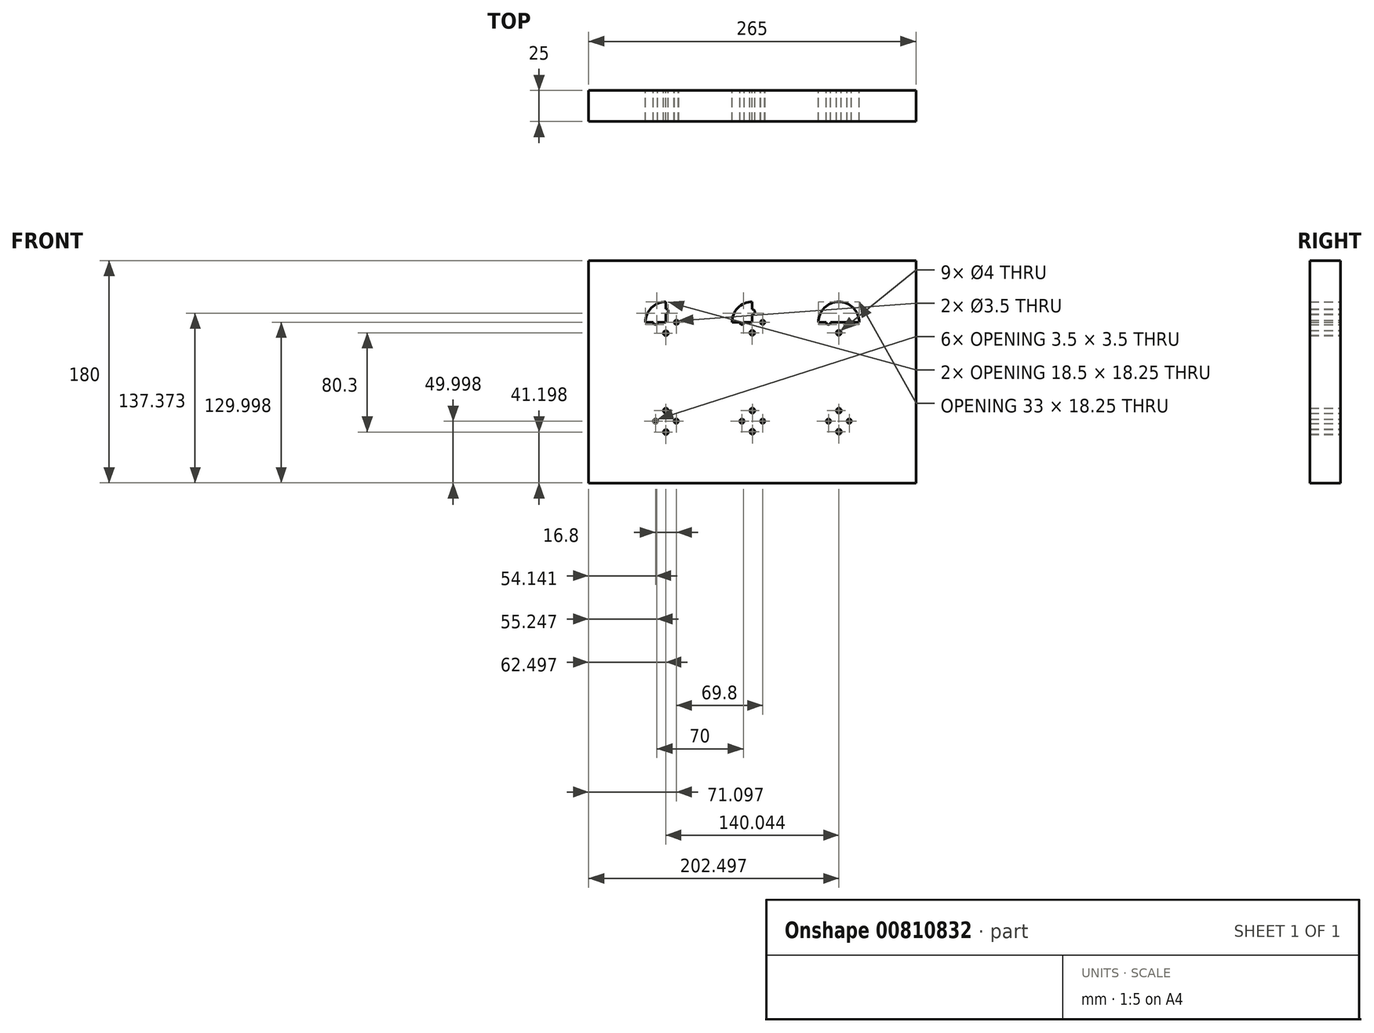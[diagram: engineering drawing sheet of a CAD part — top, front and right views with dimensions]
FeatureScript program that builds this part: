
annotation { "Feature Type Name" : "Feature", "Feature Type Description" : "" }
export const myFeature = defineFeature(function(context is Context, id is Id, definition is map)
    precondition{}
    {
        {
            var Q0;
            Q0=qCreatedBy(makeId("Front.planeOp"),FACE);
            var sketch = newSketch(context, id + "F0", { "sketchPlane" : qUnion([Q0])});
            skLineSegment(sketch, "E0.bottom", {"start": v(-104.92, 118.45) * mm, "end": v(160.08, 118.45) * mm});
            skLineSegment(sketch, "E0.top", {"start": v(-104.92, -61.55) * mm, "end": v(160.08, -61.55) * mm});
            skLineSegment(sketch, "E0.left", {"start": v(-104.92, 118.45) * mm, "end": v(-104.92, -61.55) * mm});
            skLineSegment(sketch, "E0.right", {"start": v(160.08, 118.45) * mm, "end": v(160.08, -61.55) * mm});
            skLineSegment(sketch, "E1", {"start": v(-42.42, 118.45) * mm, "end": v(-42.42, -61.55) * mm});
            skLineSegment(sketch, "E2", {"start": v(27.58, 118.45) * mm, "end": v(27.58, -61.55) * mm});
            skLineSegment(sketch, "E3", {"start": v(97.58, 118.45) * mm, "end": v(97.58, -61.55) * mm});
            skLineSegment(sketch, "E4", {"start": v(-104.92, 68.45) * mm, "end": v(160.08, 68.45) * mm});
            skLineSegment(sketch, "E5", {"start": v(-104.92, -11.55) * mm, "end": v(160.08, -11.55) * mm});
            skCircle(sketch, "E6", {"center": v(-42.42, 68.45) * mm, "radius": 16.5 * mm});
            skCircle(sketch, "E7", {"center": v(-33.82, 68.45) * mm, "radius": 1.75 * mm});
            skCircle(sketch, "E8", {"center": v(-50.82, 68.45) * mm, "radius": 1.75 * mm});
            skCircle(sketch, "E9", {"center": v(-42.42, 59.65) * mm, "radius": 2 * mm});
            skCircle(sketch, "E10", {"center": v(-42.42, 77.25) * mm, "radius": 2 * mm});
            skLineSegment(sketch, "E11.direction1", {"start": v(-42.42, 68.45) * mm, "end": v(27.58, 68.45) * mm, "construction": true});
            skLineSegment(sketch, "E11.direction2", {"start": v(-42.42, 68.45) * mm, "end": v(-42.42, -1.55) * mm, "construction": true});
            skCircle(sketch, "E12.0.1.0", {"center": v(-42.38, -11.55) * mm, "radius": 16.5 * mm});
            skCircle(sketch, "E12.0.1.1", {"center": v(-42.38, -3.05) * mm, "radius": 2 * mm});
            skCircle(sketch, "E12.0.1.2", {"center": v(-33.98, -11.55) * mm, "radius": 1.75 * mm});
            skCircle(sketch, "E12.0.1.3", {"center": v(-42.38, -20.35) * mm, "radius": 2 * mm});
            skCircle(sketch, "E12.0.1.4", {"center": v(-50.78, -11.55) * mm, "radius": 1.75 * mm});
            skCircle(sketch, "E12.1.0.0", {"center": v(27.58, 68.45) * mm, "radius": 16.5 * mm});
            skCircle(sketch, "E12.1.0.1", {"center": v(27.58, 76.95) * mm, "radius": 2 * mm});
            skCircle(sketch, "E12.1.0.2", {"center": v(35.98, 68.45) * mm, "radius": 1.75 * mm});
            skCircle(sketch, "E12.1.0.3", {"center": v(27.58, 59.95) * mm, "radius": 2 * mm});
            skCircle(sketch, "E12.1.0.4", {"center": v(19.18, 68.45) * mm, "radius": 1.75 * mm});
            skCircle(sketch, "E12.1.1.0", {"center": v(27.62, -11.55) * mm, "radius": 16.5 * mm});
            skCircle(sketch, "E12.1.1.1", {"center": v(27.62, -3.05) * mm, "radius": 2 * mm});
            skCircle(sketch, "E12.1.1.2", {"center": v(36.02, -11.55) * mm, "radius": 1.75 * mm});
            skCircle(sketch, "E12.1.1.3", {"center": v(27.62, -20.05) * mm, "radius": 2 * mm});
            skCircle(sketch, "E12.1.1.4", {"center": v(19.22, -11.55) * mm, "radius": 1.75 * mm});
            skCircle(sketch, "E12.2.0.0", {"center": v(97.58, 68.45) * mm, "radius": 16.5 * mm});
            skCircle(sketch, "E12.2.0.1", {"center": v(97.58, 76.95) * mm, "radius": 2 * mm});
            skCircle(sketch, "E12.2.0.2", {"center": v(105.98, 68.45) * mm, "radius": 1.75 * mm});
            skCircle(sketch, "E12.2.0.3", {"center": v(97.58, 59.95) * mm, "radius": 2 * mm});
            skCircle(sketch, "E12.2.0.4", {"center": v(89.18, 68.45) * mm, "radius": 1.75 * mm});
            skCircle(sketch, "E12.2.1.0", {"center": v(97.62, -11.55) * mm, "radius": 16.5 * mm});
            skCircle(sketch, "E12.2.1.1", {"center": v(97.62, -3.05) * mm, "radius": 2 * mm});
            skCircle(sketch, "E12.2.1.2", {"center": v(106.02, -11.55) * mm, "radius": 1.75 * mm});
            skCircle(sketch, "E12.2.1.3", {"center": v(97.62, -20.05) * mm, "radius": 2 * mm});
            skCircle(sketch, "E12.2.1.4", {"center": v(89.22, -11.55) * mm, "radius": 1.75 * mm});
            skLineSegment(sketch, "E12.direction2", {"start": v(-42.42, 59.65) * mm, "end": v(-42.38, -20.35) * mm, "construction": true});
            skSolve(sketch);
        }
        {
            var Q0;
            Q0 = qSketchRegion(id + "F0", true);
            var Q1;
            {var subQ5=sQuery(id+"F0.wireOp",EDGE,"E6");var subQ13=sQuery(id+"F0.wireOp",EDGE,"E1");var subQ14=makeQuery(id+"F0.imprint","INTERSECT",VERTEX,{"disambiguationData":[OD(1.0)],"derivedFrom":[subQ13,subQ5]});Q1=makeQuery(id+"F0.imprint","IMPRINT",FACE,{"disambiguationData":[TD([[makeQuery(id+"F0.imprint","IMPRINT",EDGE,{"disambiguationData":[TD([[subQ14,-1.0]])],"derivedFrom":subQ13}),1.0]])]});}
            var Q2;
            {var subQ5=sQuery(id+"F0.wireOp",EDGE,"E12.1.0.0");var subQ13=sQuery(id+"F0.wireOp",EDGE,"E2");var subQ15=makeQuery(id+"F0.imprint","INTERSECT",VERTEX,{"disambiguationData":[OD(1.0)],"derivedFrom":[subQ13,subQ5]});Q2=makeQuery(id+"F0.imprint","IMPRINT",FACE,{"disambiguationData":[TD([[makeQuery(id+"F0.imprint","IMPRINT",EDGE,{"disambiguationData":[TD([[subQ15,-1.0]])],"derivedFrom":subQ13}),1.0]])]});}
            var Q3;
            {var subQ0=sQuery(id+"F0.wireOp",EDGE,"E4");var subQ1=sQuery(id+"F0.wireOp",EDGE,"E3");var subQ2=makeQuery(id+"F0.imprint","INTERSECT",VERTEX,{"derivedFrom":[subQ1,subQ0]});Q3=makeQuery(id+"F0.imprint","IMPRINT",FACE,{"disambiguationData":[TD([[makeQuery(id+"F0.imprint","IMPRINT",EDGE,{"disambiguationData":[TD([[subQ2,-1.0]])],"derivedFrom":subQ1}),-1.0]])]});}
            var Q4;
            {var subQ1=sQuery(id+"F0.wireOp",EDGE,"E3");var subQ5=sQuery(id+"F0.wireOp",EDGE,"E12.2.0.0");var subQ10=makeQuery(id+"F0.imprint","INTERSECT",VERTEX,{"disambiguationData":[OD(0.0)],"derivedFrom":[subQ1,subQ5]});Q4=makeQuery(id+"F0.imprint","IMPRINT",FACE,{"disambiguationData":[TD([[makeQuery(id+"F0.imprint","IMPRINT",EDGE,{"disambiguationData":[TD([[subQ10,-1.0]])],"derivedFrom":subQ1}),-1.0]])]});}
            var Q5;
            {var subQ3=sQuery(id+"F0.wireOp",EDGE,"E12.2.0.0");var subQ6=sQuery(id+"F0.wireOp",EDGE,"E3");var subQ11=makeQuery(id+"F0.imprint","INTERSECT",VERTEX,{"disambiguationData":[OD(0.0)],"derivedFrom":[subQ6,subQ3]});Q5=makeQuery(id+"F0.imprint","IMPRINT",FACE,{"disambiguationData":[TD([[makeQuery(id+"F0.imprint","IMPRINT",EDGE,{"disambiguationData":[TD([[subQ11,-1.0]])],"derivedFrom":subQ6}),1.0]])]});}
            var Q6;
            {var subQ1=sQuery(id+"F0.wireOp",EDGE,"E4");var subQ5=sQuery(id+"F0.wireOp",EDGE,"E3");var subQ6=makeQuery(id+"F0.imprint","INTERSECT",VERTEX,{"derivedFrom":[subQ5,subQ1]});Q6=makeQuery(id+"F0.imprint","IMPRINT",FACE,{"disambiguationData":[TD([[makeQuery(id+"F0.imprint","IMPRINT",EDGE,{"disambiguationData":[TD([[subQ6,-1.0]])],"derivedFrom":subQ5}),1.0]])]});}
            var Q7;
            {var subQ1=sQuery(id+"F0.wireOp",EDGE,"E3");var subQ7=sQuery(id+"F0.wireOp",EDGE,"E12.2.1.0");var subQ8=makeQuery(id+"F0.imprint","INTERSECT",VERTEX,{"disambiguationData":[OD(0.0)],"derivedFrom":[subQ1,subQ7]});Q7=makeQuery(id+"F0.imprint","IMPRINT",FACE,{"disambiguationData":[TD([[makeQuery(id+"F0.imprint","IMPRINT",EDGE,{"disambiguationData":[TD([[subQ8,-1.0]])],"derivedFrom":subQ1}),-1.0]])]});}
            var Q8;
            {var subQ3=sQuery(id+"F0.wireOp",EDGE,"E12.2.1.0");var subQ5=sQuery(id+"F0.wireOp",EDGE,"E3");var subQ10=makeQuery(id+"F0.imprint","INTERSECT",VERTEX,{"disambiguationData":[OD(0.0)],"derivedFrom":[subQ5,subQ3]});Q8=makeQuery(id+"F0.imprint","IMPRINT",FACE,{"disambiguationData":[TD([[makeQuery(id+"F0.imprint","IMPRINT",EDGE,{"disambiguationData":[TD([[subQ10,-1.0]])],"derivedFrom":subQ5}),1.0]])]});}
            var Q9;
            {var subQ1=sQuery(id+"F0.wireOp",EDGE,"E5");var subQ6=sQuery(id+"F0.wireOp",EDGE,"E3");var subQ9=makeQuery(id+"F0.imprint","INTERSECT",VERTEX,{"derivedFrom":[subQ6,subQ1]});Q9=makeQuery(id+"F0.imprint","IMPRINT",FACE,{"disambiguationData":[TD([[makeQuery(id+"F0.imprint","IMPRINT",EDGE,{"disambiguationData":[TD([[subQ9,-1.0]])],"derivedFrom":subQ6}),1.0]])]});}
            var Q10;
            {var subQ0=sQuery(id+"F0.wireOp",EDGE,"E5");var subQ1=sQuery(id+"F0.wireOp",EDGE,"E3");var subQ2=makeQuery(id+"F0.imprint","INTERSECT",VERTEX,{"derivedFrom":[subQ1,subQ0]});Q10=makeQuery(id+"F0.imprint","IMPRINT",FACE,{"disambiguationData":[TD([[makeQuery(id+"F0.imprint","IMPRINT",EDGE,{"disambiguationData":[TD([[subQ2,-1.0]])],"derivedFrom":subQ1}),-1.0]])]});}
            var Q11;
            {var subQ1=sQuery(id+"F0.wireOp",EDGE,"E5");var subQ5=sQuery(id+"F0.wireOp",EDGE,"E2");var subQ6=makeQuery(id+"F0.imprint","INTERSECT",VERTEX,{"derivedFrom":[subQ5,subQ1]});Q11=makeQuery(id+"F0.imprint","IMPRINT",FACE,{"disambiguationData":[TD([[makeQuery(id+"F0.imprint","IMPRINT",EDGE,{"disambiguationData":[TD([[subQ6,-1.0]])],"derivedFrom":subQ5}),1.0]])]});}
            var Q12;
            {var subQ3=sQuery(id+"F0.wireOp",EDGE,"E12.1.1.0");var subQ6=sQuery(id+"F0.wireOp",EDGE,"E2");var subQ10=makeQuery(id+"F0.imprint","INTERSECT",VERTEX,{"disambiguationData":[OD(0.0)],"derivedFrom":[subQ6,subQ3]});Q12=makeQuery(id+"F0.imprint","IMPRINT",FACE,{"disambiguationData":[TD([[makeQuery(id+"F0.imprint","IMPRINT",EDGE,{"disambiguationData":[TD([[subQ10,-1.0]])],"derivedFrom":subQ6}),1.0]])]});}
            var Q13;
            {var subQ1=sQuery(id+"F0.wireOp",EDGE,"E2");var subQ5=sQuery(id+"F0.wireOp",EDGE,"E12.1.1.0");var subQ10=makeQuery(id+"F0.imprint","INTERSECT",VERTEX,{"disambiguationData":[OD(0.0)],"derivedFrom":[subQ1,subQ5]});Q13=makeQuery(id+"F0.imprint","IMPRINT",FACE,{"disambiguationData":[TD([[makeQuery(id+"F0.imprint","IMPRINT",EDGE,{"disambiguationData":[TD([[subQ10,-1.0]])],"derivedFrom":subQ1}),-1.0]])]});}
            var Q14;
            {var subQ0=sQuery(id+"F0.wireOp",EDGE,"E5");var subQ1=sQuery(id+"F0.wireOp",EDGE,"E2");var subQ2=makeQuery(id+"F0.imprint","INTERSECT",VERTEX,{"derivedFrom":[subQ1,subQ0]});Q14=makeQuery(id+"F0.imprint","IMPRINT",FACE,{"disambiguationData":[TD([[makeQuery(id+"F0.imprint","IMPRINT",EDGE,{"disambiguationData":[TD([[subQ2,-1.0]])],"derivedFrom":subQ1}),-1.0]])]});}
            var Q15;
            {var subQ1=sQuery(id+"F0.wireOp",EDGE,"E4");var subQ5=sQuery(id+"F0.wireOp",EDGE,"E2");var subQ6=makeQuery(id+"F0.imprint","INTERSECT",VERTEX,{"derivedFrom":[subQ5,subQ1]});Q15=makeQuery(id+"F0.imprint","IMPRINT",FACE,{"disambiguationData":[TD([[makeQuery(id+"F0.imprint","IMPRINT",EDGE,{"disambiguationData":[TD([[subQ6,-1.0]])],"derivedFrom":subQ5}),1.0]])]});}
            var Q16;
            {var subQ3=sQuery(id+"F0.wireOp",EDGE,"E12.1.0.0");var subQ5=sQuery(id+"F0.wireOp",EDGE,"E2");var subQ6=makeQuery(id+"F0.imprint","INTERSECT",VERTEX,{"disambiguationData":[OD(0.0)],"derivedFrom":[subQ5,subQ3]});Q16=makeQuery(id+"F0.imprint","IMPRINT",FACE,{"disambiguationData":[TD([[makeQuery(id+"F0.imprint","IMPRINT",EDGE,{"disambiguationData":[TD([[subQ6,-1.0]])],"derivedFrom":subQ5}),1.0]])]});}
            var Q17;
            {var subQ1=sQuery(id+"F0.wireOp",EDGE,"E2");var subQ5=sQuery(id+"F0.wireOp",EDGE,"E12.1.0.0");var subQ11=makeQuery(id+"F0.imprint","INTERSECT",VERTEX,{"disambiguationData":[OD(0.0)],"derivedFrom":[subQ1,subQ5]});Q17=makeQuery(id+"F0.imprint","IMPRINT",FACE,{"disambiguationData":[TD([[makeQuery(id+"F0.imprint","IMPRINT",EDGE,{"disambiguationData":[TD([[subQ11,-1.0]])],"derivedFrom":subQ1}),-1.0]])]});}
            var Q18;
            {var subQ0=sQuery(id+"F0.wireOp",EDGE,"E4");var subQ1=sQuery(id+"F0.wireOp",EDGE,"E2");var subQ2=makeQuery(id+"F0.imprint","INTERSECT",VERTEX,{"derivedFrom":[subQ1,subQ0]});Q18=makeQuery(id+"F0.imprint","IMPRINT",FACE,{"disambiguationData":[TD([[makeQuery(id+"F0.imprint","IMPRINT",EDGE,{"disambiguationData":[TD([[subQ2,-1.0]])],"derivedFrom":subQ1}),-1.0]])]});}
            var Q19;
            {var subQ1=sQuery(id+"F0.wireOp",EDGE,"E1");var subQ8=sQuery(id+"F0.wireOp",EDGE,"E6");var subQ10=makeQuery(id+"F0.imprint","INTERSECT",VERTEX,{"disambiguationData":[OD(0.0)],"derivedFrom":[subQ1,subQ8]});Q19=makeQuery(id+"F0.imprint","IMPRINT",FACE,{"disambiguationData":[TD([[makeQuery(id+"F0.imprint","IMPRINT",EDGE,{"disambiguationData":[TD([[subQ10,-1.0]])],"derivedFrom":subQ1}),1.0]])]});}
            var Q20;
            {var subQ1=sQuery(id+"F0.wireOp",EDGE,"E1");var subQ7=sQuery(id+"F0.wireOp",EDGE,"E6");var subQ10=makeQuery(id+"F0.imprint","INTERSECT",VERTEX,{"disambiguationData":[OD(0.0)],"derivedFrom":[subQ1,subQ7]});Q20=makeQuery(id+"F0.imprint","IMPRINT",FACE,{"disambiguationData":[TD([[makeQuery(id+"F0.imprint","IMPRINT",EDGE,{"disambiguationData":[TD([[subQ10,-1.0]])],"derivedFrom":subQ1}),-1.0]])]});}
            var Q21;
            {var subQ0=sQuery(id+"F0.wireOp",EDGE,"E4");var subQ1=sQuery(id+"F0.wireOp",EDGE,"E1");var subQ2=makeQuery(id+"F0.imprint","INTERSECT",VERTEX,{"derivedFrom":[subQ1,subQ0]});Q21=makeQuery(id+"F0.imprint","IMPRINT",FACE,{"disambiguationData":[TD([[makeQuery(id+"F0.imprint","IMPRINT",EDGE,{"disambiguationData":[TD([[subQ2,-1.0]])],"derivedFrom":subQ1}),-1.0]])]});}
            var Q22;
            {var subQ1=sQuery(id+"F0.wireOp",EDGE,"E1");var subQ8=sQuery(id+"F0.wireOp",EDGE,"E12.0.1.0");var subQ11=makeQuery(id+"F0.imprint","INTERSECT",VERTEX,{"disambiguationData":[OD(0.0)],"derivedFrom":[subQ1,subQ8]});Q22=makeQuery(id+"F0.imprint","IMPRINT",FACE,{"disambiguationData":[TD([[makeQuery(id+"F0.imprint","IMPRINT",EDGE,{"disambiguationData":[TD([[subQ11,-1.0]])],"derivedFrom":subQ1}),1.0]])]});}
            var Q23;
            {var subQ1=sQuery(id+"F0.wireOp",EDGE,"E1");var subQ7=sQuery(id+"F0.wireOp",EDGE,"E12.0.1.0");var subQ10=makeQuery(id+"F0.imprint","INTERSECT",VERTEX,{"disambiguationData":[OD(0.0)],"derivedFrom":[subQ1,subQ7]});Q23=makeQuery(id+"F0.imprint","IMPRINT",FACE,{"disambiguationData":[TD([[makeQuery(id+"F0.imprint","IMPRINT",EDGE,{"disambiguationData":[TD([[subQ10,-1.0]])],"derivedFrom":subQ1}),-1.0]])]});}
            var Q24;
            {var subQ0=sQuery(id+"F0.wireOp",EDGE,"E5");var subQ1=sQuery(id+"F0.wireOp",EDGE,"E1");var subQ2=makeQuery(id+"F0.imprint","INTERSECT",VERTEX,{"derivedFrom":[subQ1,subQ0]});Q24=makeQuery(id+"F0.imprint","IMPRINT",FACE,{"disambiguationData":[TD([[makeQuery(id+"F0.imprint","IMPRINT",EDGE,{"disambiguationData":[TD([[subQ2,-1.0]])],"derivedFrom":subQ1}),-1.0]])]});}
            var Q25;
            {var subQ1=sQuery(id+"F0.wireOp",EDGE,"E4");var subQ6=sQuery(id+"F0.wireOp",EDGE,"E1");var subQ10=makeQuery(id+"F0.imprint","INTERSECT",VERTEX,{"derivedFrom":[subQ6,subQ1]});Q25=makeQuery(id+"F0.imprint","IMPRINT",FACE,{"disambiguationData":[TD([[makeQuery(id+"F0.imprint","IMPRINT",EDGE,{"disambiguationData":[TD([[subQ10,-1.0]])],"derivedFrom":subQ6}),1.0]])]});}
            var Q26;
            {var subQ1=sQuery(id+"F0.wireOp",EDGE,"E5");var subQ6=sQuery(id+"F0.wireOp",EDGE,"E1");var subQ9=makeQuery(id+"F0.imprint","INTERSECT",VERTEX,{"derivedFrom":[subQ6,subQ1]});Q26=makeQuery(id+"F0.imprint","IMPRINT",FACE,{"disambiguationData":[TD([[makeQuery(id+"F0.imprint","IMPRINT",EDGE,{"disambiguationData":[TD([[subQ9,-1.0]])],"derivedFrom":subQ6}),1.0]])]});}
            extrude(context, id + "F1", {"entities" : qUnion([Q0, Q1, Q2, Q3, Q4, Q5, Q6, Q7, Q8, Q9, Q10, Q11, Q12, Q13, Q14, Q15, Q16, Q17, Q18, Q19, Q20, Q21, Q22, Q23, Q24, Q25, Q26]), "depth" : 25 * mm, "offsetDistance" : 25 * mm});
        }
    });
